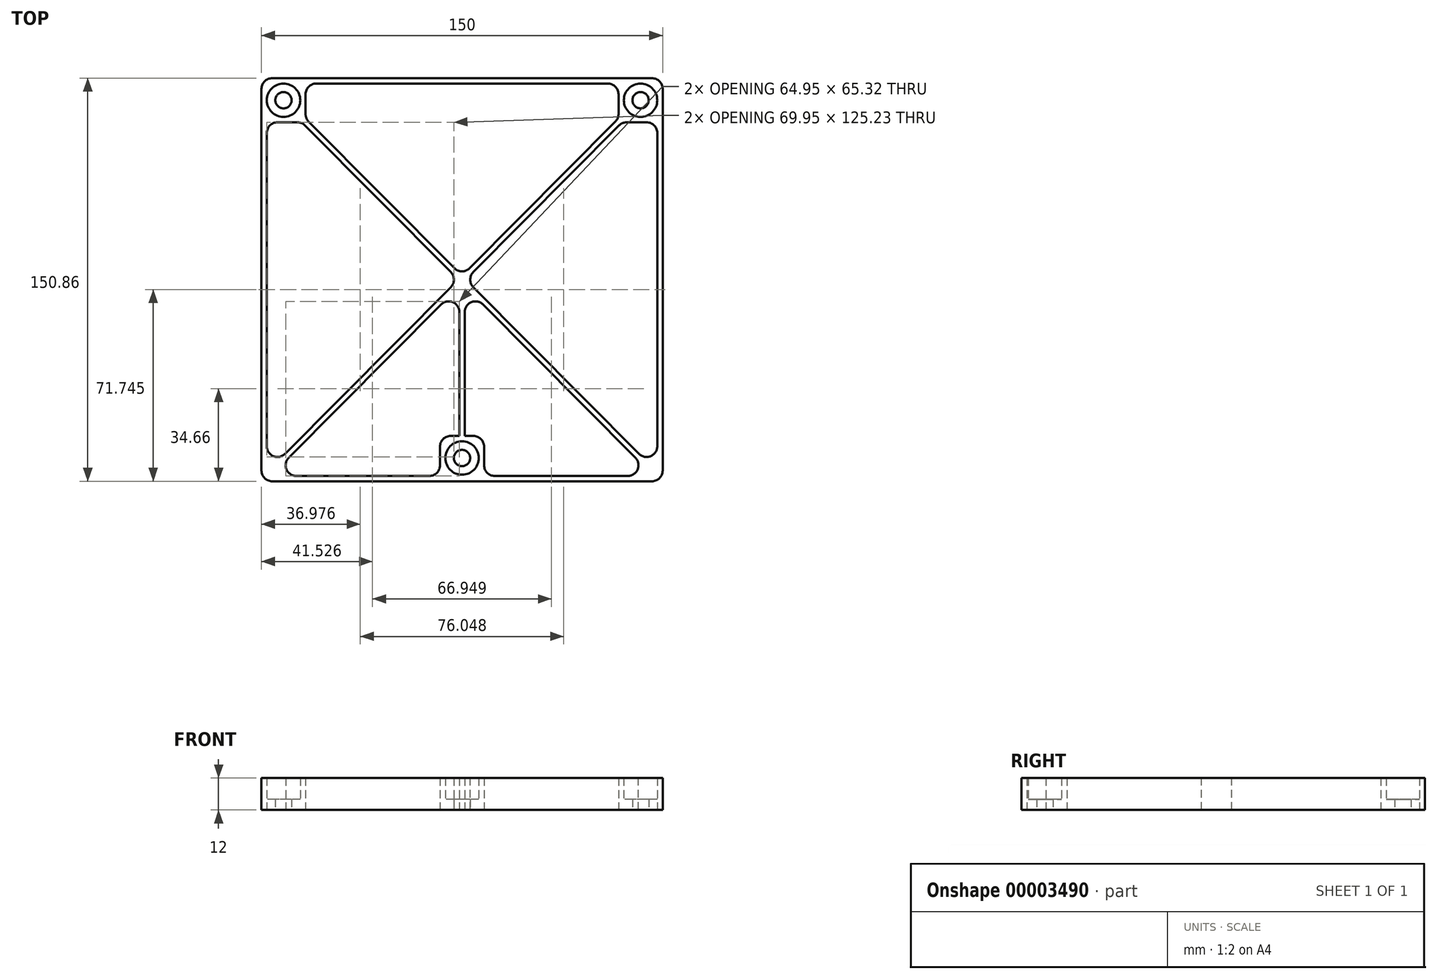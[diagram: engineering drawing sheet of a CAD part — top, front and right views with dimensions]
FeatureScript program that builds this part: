
annotation { "Feature Type Name" : "Feature", "Feature Type Description" : "" }
export const myFeature = defineFeature(function(context is Context, id is Id, definition is map)
    precondition{}
    {
        {
            var Q0;
            Q0=qCreatedBy(makeId("Top.planeOp"),FACE);
            var sketch = newSketch(context, id + "F0", { "sketchPlane" : qUnion([Q0])});
            skCircle(sketch, "E0", {"center": v(-66.75, 80.62) * mm, "radius": 6.25 * mm});
            skCircle(sketch, "E1", {"center": v(66.75, 80.62) * mm, "radius": 6.25 * mm});
            skCircle(sketch, "E2", {"center": v(0, -53.28) * mm, "radius": 6.25 * mm});
            skCircle(sketch, "E3", {"center": v(-66.75, 80.62) * mm, "radius": 3.05 * mm});
            skCircle(sketch, "E4", {"center": v(66.75, 80.62) * mm, "radius": 3.05 * mm});
            skCircle(sketch, "E5", {"center": v(0, -53.28) * mm, "radius": 3.05 * mm});
            skCircle(sketch, "E6", {"center": v(0, 65.62) * mm, "radius": 3.25 * mm});
            skLineSegment(sketch, "E7", {"start": v(0, -53.28) * mm, "end": v(0, -62) * mm, "construction": true});
            skLineSegment(sketch, "E8.rect.bottom", {"start": v(75, 88.87) * mm, "end": v(-75, 88.87) * mm});
            skLineSegment(sketch, "E8.rect.top", {"start": v(75, -62) * mm, "end": v(-75, -62) * mm});
            skLineSegment(sketch, "E8.rect.right", {"start": v(-75, 88.87) * mm, "end": v(-75, -62) * mm});
            skLineSegment(sketch, "E9", {"start": v(75, 88.87) * mm, "end": v(75, -62) * mm});
            skLineSegment(sketch, "E10", {"start": v(73, -60) * mm, "end": v(8.25, -60) * mm});
            skLineSegment(sketch, "E11", {"start": v(8.25, -60) * mm, "end": v(8.25, -45.03) * mm});
            skLineSegment(sketch, "E12", {"start": v(8.25, -45.03) * mm, "end": v(-8.25, -45.03) * mm});
            skLineSegment(sketch, "E13", {"start": v(-8.25, -45.03) * mm, "end": v(-8.25, -60) * mm});
            skLineSegment(sketch, "E14", {"start": v(-8.25, -60) * mm, "end": v(-73, -60) * mm});
            skLineSegment(sketch, "E15", {"start": v(-40.62, -60) * mm, "end": v(-40.62, -62) * mm, "construction": true});
            skLineSegment(sketch, "E16", {"start": v(40.62, -60) * mm, "end": v(40.62, -62) * mm, "construction": true});
            skLineSegment(sketch, "E17", {"start": v(-6.25, -53.28) * mm, "end": v(-8.25, -53.28) * mm, "construction": true});
            skLineSegment(sketch, "E18", {"start": v(-73, -60) * mm, "end": v(-73, 72.37) * mm});
            skLineSegment(sketch, "E19", {"start": v(-73, 72.37) * mm, "end": v(-58.5, 72.37) * mm});
            skLineSegment(sketch, "E20", {"start": v(-58.5, 72.37) * mm, "end": v(-58.5, 86.87) * mm});
            skLineSegment(sketch, "E21", {"start": v(-58.5, 86.87) * mm, "end": v(58.5, 86.87) * mm});
            skLineSegment(sketch, "E22", {"start": v(58.5, 86.87) * mm, "end": v(58.5, 72.37) * mm});
            skLineSegment(sketch, "E23", {"start": v(58.5, 72.37) * mm, "end": v(73, 72.37) * mm});
            skLineSegment(sketch, "E24", {"start": v(73, 72.37) * mm, "end": v(73, -60) * mm});
            skLineSegment(sketch, "E25", {"start": v(-73, -6.33) * mm, "end": v(-75, -6.33) * mm, "construction": true});
            skLineSegment(sketch, "E26", {"start": v(-66.75, 74.37) * mm, "end": v(-66.75, 72.37) * mm, "construction": true});
            skLineSegment(sketch, "E27", {"start": v(66.75, 74.37) * mm, "end": v(66.75, 72.37) * mm, "construction": true});
            skLineSegment(sketch, "E28", {"start": v(73, -4.32) * mm, "end": v(75, -4.32) * mm, "construction": true});
            skLineSegment(sketch, "E29", {"start": v(0, 68.87) * mm, "end": v(0, 88.87) * mm, "construction": true});
            skLineSegment(sketch, "E30", {"start": v(60.5, 80.62) * mm, "end": v(58.5, 80.62) * mm, "construction": true});
            skLineSegment(sketch, "E31", {"start": v(-60.5, 80.62) * mm, "end": v(-58.5, 80.62) * mm, "construction": true});
            skLineSegment(sketch, "E32", {"start": v(0, 0) * mm, "end": v(-73, 0) * mm, "construction": true});
            skLineSegment(sketch, "E33", {"start": v(0, 0) * mm, "end": v(73, 0) * mm, "construction": true});
            skLineSegment(sketch, "E34", {"start": v(-13.4, 86.87) * mm, "end": v(-13.4, 88.87) * mm, "construction": true});
            skLineSegment(sketch, "E35", {"start": v(-58.5, 73.78) * mm, "end": v(0, 14.9) * mm});
            skLineSegment(sketch, "E36", {"start": v(-59.92, 72.37) * mm, "end": v(-1.4, 13.48) * mm});
            skLineSegment(sketch, "E37", {"start": v(-33.58, 45.86) * mm, "end": v(-32.16, 47.27) * mm, "construction": true});
            skLineSegment(sketch, "E38", {"start": v(-59.92, 72.37) * mm, "end": v(-58.5, 73.78) * mm, "construction": true});
            skLineSegment(sketch, "E39", {"start": v(71.58, -60) * mm, "end": v(73, -58.58) * mm, "construction": true});
            skLineSegment(sketch, "E40", {"start": v(-73, -58.58) * mm, "end": v(-1.4, 13.48) * mm});
            skLineSegment(sketch, "E41", {"start": v(59.92, 72.37) * mm, "end": v(1.4, 13.48) * mm});
            skLineSegment(sketch, "E42", {"start": v(21.22, 36.26) * mm, "end": v(22.64, 34.85) * mm, "construction": true});
            skLineSegment(sketch, "E43", {"start": v(58.5, 73.78) * mm, "end": v(59.92, 72.37) * mm, "construction": true});
            skLineSegment(sketch, "E44", {"start": v(-71.58, -60) * mm, "end": v(-73, -58.58) * mm, "construction": true});
            skLineSegment(sketch, "E45.trimOffspring", {"start": v(-1, 11.05) * mm, "end": v(-71.58, -60) * mm});
            skLineSegment(sketch, "E46.trimOffspring", {"start": v(1, 11.05) * mm, "end": v(71.58, -60) * mm});
            skLineSegment(sketch, "E47.trimOffspring", {"start": v(0, 14.9) * mm, "end": v(58.5, 73.78) * mm});
            skLineSegment(sketch, "E48.trimOffspring", {"start": v(1.4, 13.48) * mm, "end": v(73, -58.58) * mm});
            skLineSegment(sketch, "E49", {"start": v(0, -47.03) * mm, "end": v(0, -45.03) * mm, "construction": true});
            skLineSegment(sketch, "E50", {"start": v(6.25, -53.28) * mm, "end": v(8.25, -53.28) * mm, "construction": true});
            skLineSegment(sketch, "E51", {"start": v(1, -45.03) * mm, "end": v(1, 11.05) * mm});
            skLineSegment(sketch, "E52", {"start": v(-1, 11.05) * mm, "end": v(-1, -45.03) * mm});
            skLineSegment(sketch, "E53", {"start": v(-1, -16.99) * mm, "end": v(1, -16.99) * mm, "construction": true});
            skLineSegment(sketch, "E54", {"start": v(-1, -32.36) * mm, "end": v(-44.13, -32.36) * mm, "construction": true});
            skLineSegment(sketch, "E55", {"start": v(1, -32.36) * mm, "end": v(44.13, -32.36) * mm, "construction": true});
            skLineSegment(sketch, "E56", {"start": v(-73, 80.62) * mm, "end": v(-75, 80.62) * mm, "construction": true});
            skLineSegment(sketch, "E57", {"start": v(-66.75, 86.87) * mm, "end": v(-66.75, 88.87) * mm, "construction": true});
            skLineSegment(sketch, "E58", {"start": v(66.75, 86.87) * mm, "end": v(66.75, 88.87) * mm, "construction": true});
            skLineSegment(sketch, "E59", {"start": v(73, 80.62) * mm, "end": v(75, 80.62) * mm, "construction": true});
            skSolve(sketch);
        }
        {
            var Q0;
            Q0=makeQuery(id+"F0.imprint","IMPRINT",FACE,{"disambiguationData":[TD([[makeQuery(id+"F0.imprint","IMPRINT",EDGE,{"derivedFrom":sQuery(id+"F0.wireOp",EDGE,"E8.rect.bottom")}),1.0]])]});
            var Q1;
            {var subQ9=sQuery(id+"F0.wireOp",EDGE,"E35");Q1=makeQuery(id+"F0.imprint","IMPRINT",FACE,{"disambiguationData":[TD([[makeQuery(id+"F0.imprint","IMPRINT",EDGE,{"derivedFrom":subQ9}),-1.0]])]});}
            var Q2;
            Q2=makeQuery(id+"F0.imprint","IMPRINT",FACE,{"disambiguationData":[TD([[makeQuery(id+"F0.imprint","IMPRINT",EDGE,{"derivedFrom":sQuery(id+"F0.wireOp",EDGE,"E2")}),-1.0]])]});
            var Q3;
            {var subQ15=sQuery(id+"F0.wireOp",EDGE,"E40");Q3=makeQuery(id+"F0.imprint","IMPRINT",FACE,{"disambiguationData":[TD([[makeQuery(id+"F0.imprint","IMPRINT",EDGE,{"derivedFrom":subQ15}),-1.0]])]});}
            var Q4;
            {var subQ5=sQuery(id+"F0.wireOp",EDGE,"E22");var subQ7=sQuery(id+"F0.wireOp",EDGE,"E23");var subQ9=makeQuery(id+"F0.imprint","INTERSECT",VERTEX,{"derivedFrom":[subQ5,subQ7]});Q4=makeQuery(id+"F0.imprint","IMPRINT",FACE,{"disambiguationData":[TD([[makeQuery(id+"F0.imprint","IMPRINT",EDGE,{"disambiguationData":[TD([[subQ9,1.0]])],"derivedFrom":subQ5}),-1.0]])]});}
            extrude(context, id + "F1", {"entities" : qUnion([Q0, Q1, Q2, Q3, Q4]), "depth" : 12 * mm});
        }
        {
            var Q0;
            Q0=makeQuery(id+"F0.imprint","IMPRINT",FACE,{"disambiguationData":[TD([[makeQuery(id+"F0.imprint","IMPRINT",EDGE,{"derivedFrom":sQuery(id+"F0.wireOp",EDGE,"E0")}),1.0]])]});
            var Q1;
            Q1=makeQuery(id+"F0.imprint","IMPRINT",FACE,{"disambiguationData":[TD([[makeQuery(id+"F0.imprint","IMPRINT",EDGE,{"derivedFrom":sQuery(id+"F0.wireOp",EDGE,"E1")}),1.0]])]});
            var Q2;
            Q2=makeQuery(id+"F0.imprint","IMPRINT",FACE,{"disambiguationData":[TD([[makeQuery(id+"F0.imprint","IMPRINT",EDGE,{"derivedFrom":sQuery(id+"F0.wireOp",EDGE,"E2")}),1.0]])]});
            extrude(context, id + "F2", {"entities" : qUnion([Q0, Q1, Q2]), "operationType" : NewBodyOperationType.ADD, "depth" : 4 * mm});
        }
        {
            var Q0;
            Q0=makeQuery(id+"F1.opExtrude","SWEPT_EDGE",EDGE,{"disambiguationData":[OSD([sQuery(id+"F0.wireOp",EDGE,"E8.rect.bottom"),sQuery(id+"F0.wireOp",EDGE,"E8.rect.right")])]});
            var Q1;
            Q1=makeQuery(id+"F1.opExtrude","SWEPT_EDGE",EDGE,{"disambiguationData":[OSD([sQuery(id+"F0.wireOp",EDGE,"E8.rect.bottom"),sQuery(id+"F0.wireOp",EDGE,"E9")])]});
            var Q2;
            Q2=makeQuery(id+"F1.opExtrude","SWEPT_EDGE",EDGE,{"disambiguationData":[OSD([sQuery(id+"F0.wireOp",EDGE,"E8.rect.top"),sQuery(id+"F0.wireOp",EDGE,"E9")])]});
            var Q3;
            Q3=makeQuery(id+"F1.opExtrude","SWEPT_EDGE",EDGE,{"disambiguationData":[OSD([sQuery(id+"F0.wireOp",EDGE,"E21"),sQuery(id+"F0.wireOp",EDGE,"7269ead7-ed49-476f-a8e7-ab20f978d723")])]});
            var Q4;
            Q4=makeQuery(id+"F1.opExtrude","SWEPT_EDGE",EDGE,{"disambiguationData":[OSD([sQuery(id+"F0.wireOp",EDGE,"7269ead7-ed49-476f-a8e7-ab20f978d723"),sQuery(id+"F0.wireOp",EDGE,"3c2d1e0e-e713-45f3-bbe7-c784489b6541")])]});
            var Q5;
            Q5=makeQuery(id+"F1.opExtrude","SWEPT_EDGE",EDGE,{"disambiguationData":[OSD([sQuery(id+"F0.wireOp",EDGE,"E8.rect.top"),sQuery(id+"F0.wireOp",EDGE,"E8.rect.right")])]});
            var Q6;
            Q6=makeQuery(id+"F1.opExtrude","SWEPT_EDGE",EDGE,{"disambiguationData":[OSD([sQuery(id+"F0.wireOp",EDGE,"E12"),sQuery(id+"F0.wireOp",EDGE,"E13")])]});
            var Q7;
            Q7=makeQuery(id+"F1.opExtrude","SWEPT_EDGE",EDGE,{"disambiguationData":[OSD([sQuery(id+"F0.wireOp",EDGE,"E22"),sQuery(id+"F0.wireOp",EDGE,"E23")])]});
            var Q8;
            Q8=makeQuery(id+"F1.opExtrude","SWEPT_EDGE",EDGE,{"disambiguationData":[OSD([sQuery(id+"F0.wireOp",EDGE,"3c2d1e0e-e713-45f3-bbe7-c784489b6541"),sQuery(id+"F0.wireOp",EDGE,"5722d2f1-9564-450d-b4c3-68423f85255b")])]});
            var Q9;
            Q9=makeQuery(id+"F1.opExtrude","SWEPT_EDGE",EDGE,{"disambiguationData":[OSD([sQuery(id+"F0.wireOp",EDGE,"3025d024-c0f1-4f40-92ef-415b047fb0c6"),sQuery(id+"F0.wireOp",EDGE,"E22")])]});
            var Q10;
            Q10=makeQuery(id+"F1.opExtrude","SWEPT_EDGE",EDGE,{"disambiguationData":[OSD([sQuery(id+"F0.wireOp",EDGE,"E23"),sQuery(id+"F0.wireOp",EDGE,"E24")])]});
            var Q11;
            Q11=makeQuery(id+"F1.opExtrude","SWEPT_EDGE",EDGE,{"disambiguationData":[OSD([sQuery(id+"F0.wireOp",EDGE,"E19"),sQuery(id+"F0.wireOp",EDGE,"E20")])]});
            var Q12;
            Q12=makeQuery(id+"F1.opExtrude","SWEPT_EDGE",EDGE,{"disambiguationData":[OSD([sQuery(id+"F0.wireOp",EDGE,"E10"),sQuery(id+"F0.wireOp",EDGE,"E24")])]});
            var Q13;
            Q13=makeQuery(id+"F1.opExtrude","SWEPT_EDGE",EDGE,{"disambiguationData":[OSD([sQuery(id+"F0.wireOp",EDGE,"E13"),sQuery(id+"F0.wireOp",EDGE,"E14")])]});
            var Q14;
            Q14=makeQuery(id+"F1.opExtrude","SWEPT_EDGE",EDGE,{"disambiguationData":[OSD([sQuery(id+"F0.wireOp",EDGE,"E11"),sQuery(id+"F0.wireOp",EDGE,"E12")])]});
            var Q15;
            Q15=makeQuery(id+"F1.opExtrude","SWEPT_EDGE",EDGE,{"disambiguationData":[OSD([sQuery(id+"F0.wireOp",EDGE,"5722d2f1-9564-450d-b4c3-68423f85255b"),sQuery(id+"F0.wireOp",EDGE,"3025d024-c0f1-4f40-92ef-415b047fb0c6")])]});
            var Q16;
            Q16=makeQuery(id+"F1.opExtrude","SWEPT_EDGE",EDGE,{"disambiguationData":[OSD([sQuery(id+"F0.wireOp",EDGE,"E20"),sQuery(id+"F0.wireOp",EDGE,"E21")])]});
            var Q17;
            Q17=makeQuery(id+"F1.opExtrude","SWEPT_EDGE",EDGE,{"disambiguationData":[OSD([sQuery(id+"F0.wireOp",EDGE,"E10"),sQuery(id+"F0.wireOp",EDGE,"E11")])]});
            var Q18;
            Q18=makeQuery(id+"F1.opExtrude","SWEPT_EDGE",EDGE,{"disambiguationData":[OSD([sQuery(id+"F0.wireOp",EDGE,"E18"),sQuery(id+"F0.wireOp",EDGE,"E19")])]});
            var Q19;
            Q19=makeQuery(id+"F1.opExtrude","SWEPT_EDGE",EDGE,{"disambiguationData":[OSD([sQuery(id+"F0.wireOp",EDGE,"E14"),sQuery(id+"F0.wireOp",EDGE,"E18")])]});
            var Q20;
            Q20=makeQuery(id+"F1.opExtrude","SWEPT_EDGE",EDGE,{"disambiguationData":[OSD([sQuery(id+"F0.wireOp",EDGE,"E45.trimOffspring"),sQuery(id+"F0.wireOp",EDGE,"E46.trimOffspring")])]});
            var Q21;
            Q21=makeQuery(id+"F1.opExtrude","SWEPT_EDGE",EDGE,{"disambiguationData":[OSD([sQuery(id+"F0.wireOp",EDGE,"E41"),sQuery(id+"F0.wireOp",EDGE,"E48.trimOffspring")])]});
            var Q22;
            Q22=makeQuery(id+"F1.opExtrude","SWEPT_EDGE",EDGE,{"disambiguationData":[OSD([sQuery(id+"F0.wireOp",EDGE,"E36"),sQuery(id+"F0.wireOp",EDGE,"E40")])]});
            var Q23;
            Q23=makeQuery(id+"F1.opExtrude","SWEPT_EDGE",EDGE,{"disambiguationData":[OSD([sQuery(id+"F0.wireOp",EDGE,"E35"),sQuery(id+"F0.wireOp",EDGE,"E47.trimOffspring")])]});
            fillet(context, id + "F3", {"entities" : qUnion([Q0, Q1, Q2, Q3, Q4, Q5, Q6, Q7, Q8, Q9, Q10, Q11, Q12, Q13, Q14, Q15, Q16, Q17, Q18, Q19, Q20, Q21, Q22, Q23]), "radius" : 4 * mm, "tangentPropagation" : true, "allowEdgeOverflow" : false});
        }
    });
